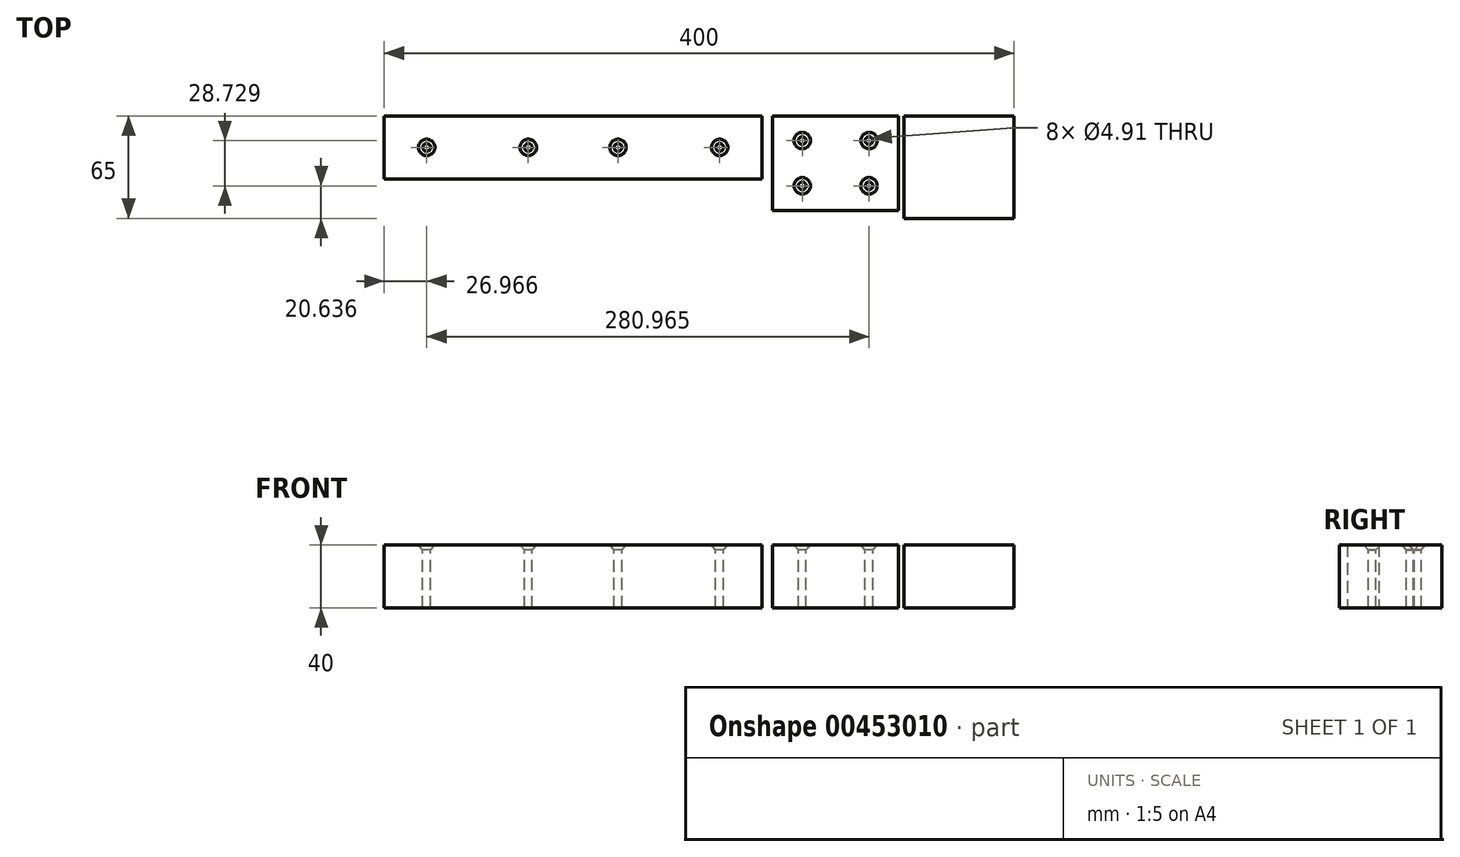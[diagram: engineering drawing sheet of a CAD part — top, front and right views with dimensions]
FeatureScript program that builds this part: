
annotation { "Feature Type Name" : "Feature", "Feature Type Description" : "" }
export const myFeature = defineFeature(function(context is Context, id is Id, definition is map)
    precondition{}
    {
        {
            var Q0;
            Q0=qCreatedBy(makeId("Top.planeOp"),FACE);
            var sketch = newSketch(context, id + "F0", { "sketchPlane" : qUnion([Q0])});
            skLineSegment(sketch, "E0.bottom", {"start": v(200, 32.5) * mm, "end": v(-200, 32.5) * mm, "construction": true});
            skLineSegment(sketch, "E0.top", {"start": v(200, -32.5) * mm, "end": v(-200, -32.5) * mm, "construction": true});
            skLineSegment(sketch, "E0.left", {"start": v(200, 32.5) * mm, "end": v(200, -32.5) * mm, "construction": true});
            skLineSegment(sketch, "E0.right", {"start": v(-200, 32.5) * mm, "end": v(-200, -32.5) * mm, "construction": true});
            skPoint(sketch, "E0.middle", {"position": v(0, 0) * mm});
            skLineSegment(sketch, "E1.bottom", {"start": v(-200, 32.5) * mm, "end": v(40, 32.5) * mm});
            skLineSegment(sketch, "E1.top", {"start": v(-200, -7.5) * mm, "end": v(40, -7.5) * mm});
            skLineSegment(sketch, "E1.left", {"start": v(-200, 32.5) * mm, "end": v(-200, -7.5) * mm});
            skLineSegment(sketch, "E1.right", {"start": v(40, 32.5) * mm, "end": v(40, -7.5) * mm});
            skLineSegment(sketch, "E2.bottom", {"start": v(46.73, 32.5) * mm, "end": v(126.73, 32.5) * mm});
            skLineSegment(sketch, "E2.top", {"start": v(46.73, -27.5) * mm, "end": v(126.73, -27.5) * mm});
            skLineSegment(sketch, "E2.left", {"start": v(46.73, 32.5) * mm, "end": v(46.73, -27.5) * mm});
            skLineSegment(sketch, "E2.right", {"start": v(126.73, 32.5) * mm, "end": v(126.73, -27.5) * mm});
            skLineSegment(sketch, "E3.bottom", {"start": v(130, 32.5) * mm, "end": v(200, 32.5) * mm});
            skLineSegment(sketch, "E3.top", {"start": v(130, -32.5) * mm, "end": v(200, -32.5) * mm});
            skLineSegment(sketch, "E3.left", {"start": v(130, 32.5) * mm, "end": v(130, -32.5) * mm});
            skLineSegment(sketch, "E3.right", {"start": v(200, 32.5) * mm, "end": v(200, -32.5) * mm});
            skSolve(sketch);
        }
        {
            var Q0;
            Q0 = qSketchRegion(id + "F0", true);
            extrude(context, id + "F1", {"entities" : qUnion([Q0]), "depth" : 40 * mm});
        }
        {
            var Q0;
            Q0=makeQuery(id+"F1.opExtrude","CAP_FACE",FACE,{"disambiguationData":[OSD([sQuery(id+"F0.wireOp",EDGE,"E1.bottom"),sQuery(id+"F0.wireOp",EDGE,"E1.top"),sQuery(id+"F0.wireOp",EDGE,"E1.left"),sQuery(id+"F0.wireOp",EDGE,"E1.right")])],"isStart":false});
            var sketch = newSketch(context, id + "F2", { "sketchPlane" : qUnion([Q0])});
            skPoint(sketch, "E4", {"position": v(-173.03, 12.5) * mm});
            skPoint(sketch, "E5", {"position": v(-108.48, 12.5) * mm});
            skPoint(sketch, "E6", {"position": v(-51.52, 12.5) * mm});
            skPoint(sketch, "E7", {"position": v(13.03, 12.5) * mm});
            skLineSegment(sketch, "E8", {"start": v(-80, 32.5) * mm, "end": v(-80, -7.5) * mm, "construction": true});
            skLineSegment(sketch, "E9", {"start": v(-108.48, 12.5) * mm, "end": v(-51.52, 12.5) * mm, "construction": true});
            skLineSegment(sketch, "E10.0.0", {"start": v(46.73, 32.5) * mm, "end": v(46.73, -27.5) * mm, "construction": true});
            skLineSegment(sketch, "E10.0.1", {"start": v(46.73, -27.5) * mm, "end": v(126.73, -27.5) * mm, "construction": true});
            skLineSegment(sketch, "E10.0.2", {"start": v(126.73, -27.5) * mm, "end": v(126.73, 32.5) * mm, "construction": true});
            skLineSegment(sketch, "E10.0.3", {"start": v(126.73, 32.5) * mm, "end": v(46.73, 32.5) * mm, "construction": true});
            skLineSegment(sketch, "E11.bottom", {"start": v(107.93, 16.86) * mm, "end": v(65.52, 16.86) * mm, "construction": true});
            skLineSegment(sketch, "E11.top", {"start": v(107.93, -11.86) * mm, "end": v(65.52, -11.86) * mm, "construction": true});
            skLineSegment(sketch, "E11.left", {"start": v(107.93, 16.86) * mm, "end": v(107.93, -11.86) * mm, "construction": true});
            skLineSegment(sketch, "E11.right", {"start": v(65.52, 16.86) * mm, "end": v(65.52, -11.86) * mm, "construction": true});
            skPoint(sketch, "E11.middle", {"position": v(86.73, 2.5) * mm});
            skPoint(sketch, "E11.middle.positionSnap0", {"position": v(46.73, 2.5) * mm});
            skPoint(sketch, "E11.middle.positionSnap1", {"position": v(86.73, 32.5) * mm});
            skPoint(sketch, "E11.centerSnap0", {"position": v(46.73, 2.5) * mm});
            skPoint(sketch, "E11.centerSnap1", {"position": v(86.73, 32.5) * mm});
            skSolve(sketch);
        }
        {
            var Q0;
            Q0=sQuery(id+"F2.wireOp",VERTEX,"E11.right.start");
            var Q1;
            Q1=sQuery(id+"F2.wireOp",VERTEX,"E11.left.start");
            var Q2;
            Q2=sQuery(id+"F2.wireOp",VERTEX,"E11.top.start");
            var Q3;
            Q3=sQuery(id+"F2.wireOp",VERTEX,"E11.top.end");
            var Q4;
            Q4=sQuery(id+"F2.wireOp",VERTEX,"E6");
            var Q5;
            Q5=sQuery(id+"F2.wireOp",VERTEX,"E7");
            var Q6;
            Q6=sQuery(id+"F2.wireOp",VERTEX,"E5");
            var Q7;
            Q7=sQuery(id+"F2.wireOp",VERTEX,"E4");
            var Q8;
            Q8=makeQuery(id+"F1.opExtrude","SWEPT_BODY",BODY,{"disambiguationData":[OSD([sQuery(id+"F0.wireOp",EDGE,"E2.bottom"),sQuery(id+"F0.wireOp",EDGE,"E2.top"),sQuery(id+"F0.wireOp",EDGE,"E2.left"),sQuery(id+"F0.wireOp",EDGE,"E2.right")])]});
            var Q9;
            Q9=makeQuery(id+"F1.opExtrude","SWEPT_BODY",BODY,{"disambiguationData":[OSD([sQuery(id+"F0.wireOp",EDGE,"E1.bottom"),sQuery(id+"F0.wireOp",EDGE,"E1.top"),sQuery(id+"F0.wireOp",EDGE,"E1.left"),sQuery(id+"F0.wireOp",EDGE,"E1.right")])]});
            hole(context, id + "F3", {"style" : HoleStyle.C_SINK, "endStyle" : HoleEndStyle.THROUGH, "standardTappedOrClearance" : lookupTablePath({ "standard" : "ANSI", "size" : "#10 (0.2)", "type" : "Drilled" }), "standardBlindInLast" : lookupTablePath({ "standard" : "ANSI", "size" : "#10", "type" : "Drilled" }), "holeDiameter" : 4.9 * mm, "cSinkDiameter" : 10.44 * mm, "cSinkAngle" : 82 * degree, "isTappedThrough" : true, "tappedDepth" : 12 * mm, "tapClearance" : 3, "locations" : qUnion([Q0, Q1, Q2, Q3, Q4, Q5, Q6, Q7]), "scope" : qUnion([Q8, Q9])});
        }
    });
